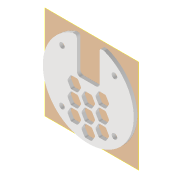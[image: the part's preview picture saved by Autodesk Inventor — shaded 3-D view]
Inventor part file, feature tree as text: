
AUTODESK INVENTOR PART (.ipt)
format: ipt  version: 2022 (Build 260153000, 153)  size: 283,648 bytes
history: native  units: mm
features: reference x6, extrude x3, sketch x3, plane x2, projected_geometry x2, other x2, hole x1, fillet x1, pattern_linear x1
ambient origin geometry x8: Origin, YZ Plane, XZ Plane, XY Plane, X Axis, Y Axis, Z Axis, Center Point
bodies: Volumenkörper1 (feature_tree)
feature tree (21):
  plane  "Arbeitsebene1"
  extrude  "Extrusion1"  Depth=4.0mm
  plane  "Arbeitsebene2"
  hole  "Bohrung1"  [1 undecoded]
  extrude  "Extrusion2"  Depth=2.0mm
  fillet  "Rundung1"  Radius=4.0mm
  extrude  "Extrusion3"  TaperAngle=0.0deg  [1 undecoded]
  pattern_linear  "Rechteckige Anordnung1"  Count1=3 Spacing1=8.0mm
  sketch  "Skizze1"  dims[d0=4.0mm d1=4.0mm]
  reference  "Referenz1"
  sketch  "Skizze2"  dims[d2=2.0mm d3=0.0mm]
  projected_geometry  "Projizierte Kontur1"
  reference  "Referenz2"
  reference  "Referenz3"
  reference  "Referenz4"
  reference  "Referenz5"
  reference  "Referenz6"
  sketch  "Skizze4"  dims[d4=3.2mm d5=6.0mm d6=4.0mm d7=2.0mm d8=90.0deg d9=8.0mm d10=20.594885mm d11=10.0mm d12=0.0mm d13=2.0mm d23=7.0mm d27=4.0mm d28=0.0mm d29=30.0mm d31=8.0mm d38=8.0mm d39=1.0mm d40=8.0mm d41=1.0mm d42=8.0mm d43=1.0mm d44=4.0mm d45=8.0mm d46=4.0mm d47=8.0mm d48=13.0mm d49=6.5mm]
  projected_geometry  "Projizierte Kontur2"
  other  "Assembly_Cube_SEEED_Xiao_Sense_Camera_v3.iam"
  other  "20_Cube_Insert_SEEED_Xiao_Sense_Camera:1"
note: 2 required parameter values undecoded (feature->parameter linkage not recoverable at this tier; creation-order binding heuristic only, values carry confidence <= 0.55)
